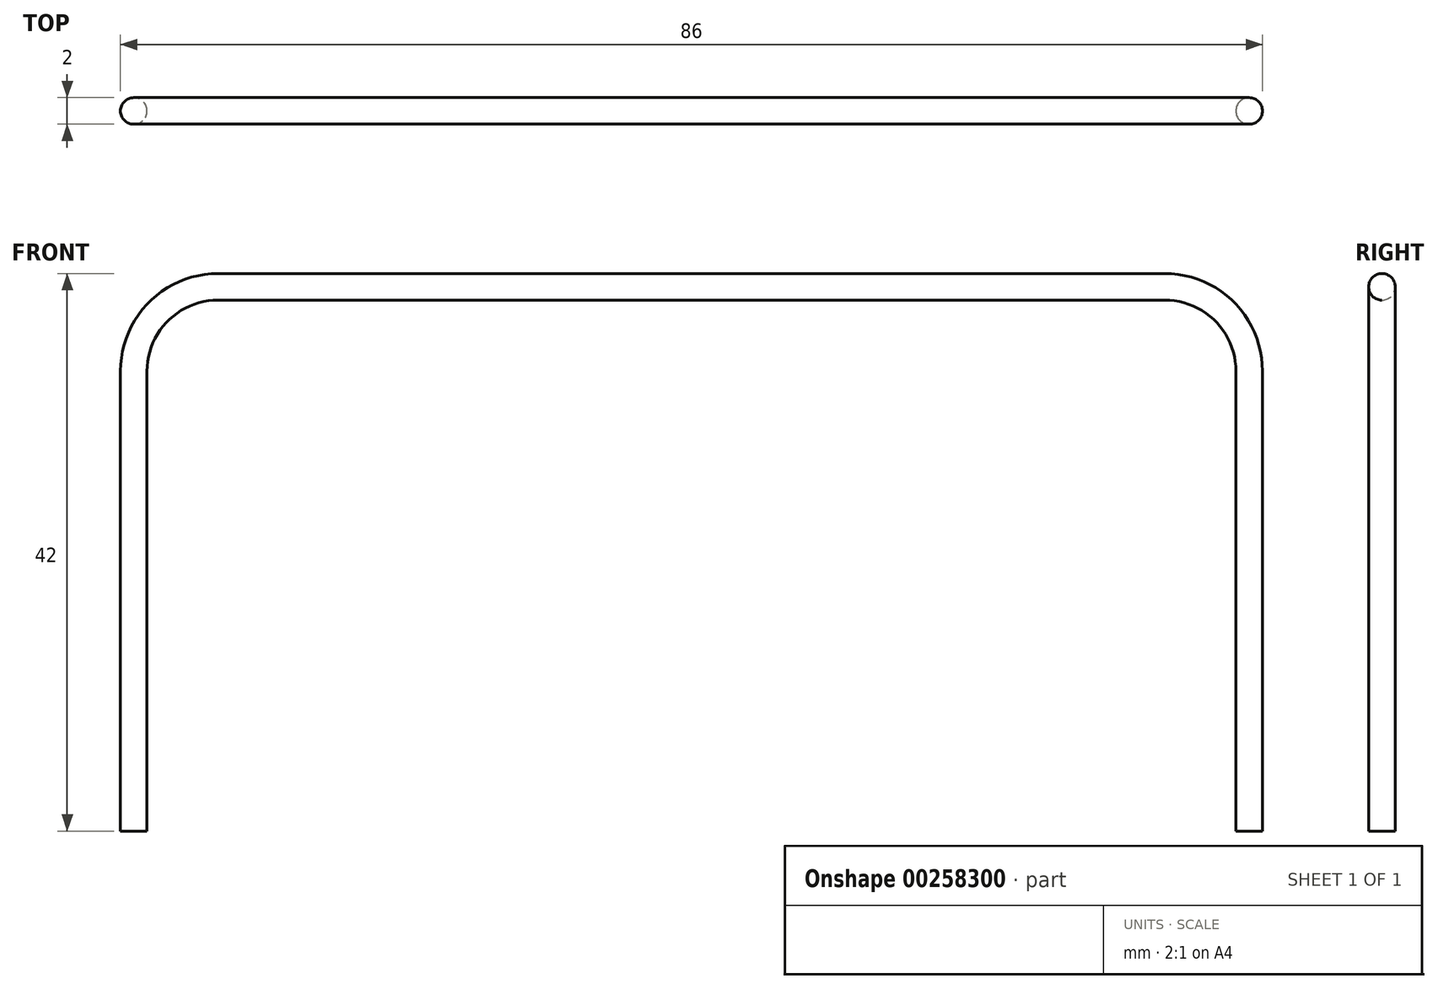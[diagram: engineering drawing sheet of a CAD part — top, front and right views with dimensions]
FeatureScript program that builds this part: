
annotation { "Feature Type Name" : "Feature", "Feature Type Description" : "" }
export const myFeature = defineFeature(function(context is Context, id is Id, definition is map)
    precondition{}
    {
        {
            var Q0;
            Q0=qCreatedBy(makeId("Front.planeOp"),FACE);
            var sketch = newSketch(context, id + "F0", { "sketchPlane" : qUnion([Q0])});
            skLineSegment(sketch, "E0", {"start": v(-42, 0) * mm, "end": v(-42, 34.65) * mm});
            skLineSegment(sketch, "E1", {"start": v(-35.65, 41) * mm, "end": v(0, 41) * mm});
            skPoint(sketch, "E2.visualSharp", {"position": v(-42, 41) * mm});
            skArc(sketch, "E2.filletArc", {"start": v(-35.65, 41) * mm, "mid": v(-40.14, 39.14) * mm, "end": v(-42, 34.65) * mm});
            skLineSegment(sketch, "E3.MirrorCS", {"start": v(35.65, 41) * mm, "end": v(0, 41) * mm});
            skArc(sketch, "E4.MirrorCS", {"start": v(35.65, 41) * mm, "mid": v(40.14, 39.14) * mm, "end": v(42, 34.65) * mm});
            skLineSegment(sketch, "E5.MirrorCS", {"start": v(42, 0) * mm, "end": v(42, 34.65) * mm});
            skSolve(sketch);
        }
        {
            var Q0;
            Q0=qCreatedBy(makeId("Top.planeOp"),FACE);
            var sketch = newSketch(context, id + "F1", { "sketchPlane" : qUnion([Q0])});
            skCircle(sketch, "E6", {"center": v(-42, 0) * mm, "radius": 1 * mm});
            skSolve(sketch);
        }
        {
            var Q0;
            Q0=makeQuery(id+"F1.imprint","IMPRINT",FACE,{"disambiguationData":[TD([[makeQuery(id+"F1.imprint","IMPRINT",EDGE,{"derivedFrom":sQuery(id+"F1.wireOp",EDGE,"E6")}),1.0]])]});
            var Q1;
            Q1=sQuery(id+"F0.wireOp",EDGE,"E0");
            var Q2;
            Q2=sQuery(id+"F0.wireOp",EDGE,"E2.filletArc");
            var Q3;
            Q3=sQuery(id+"F0.wireOp",EDGE,"E1");
            var Q4;
            Q4=sQuery(id+"F0.wireOp",EDGE,"E3.MirrorCS");
            var Q5;
            Q5=sQuery(id+"F0.wireOp",EDGE,"E4.MirrorCS");
            var Q6;
            Q6=sQuery(id+"F0.wireOp",EDGE,"E5.MirrorCS");
            sweep(context, id + "F2", {"profiles" : qUnion([Q0]), "path" : qUnion([Q1, Q2, Q3, Q4, Q5, Q6])});
        }
    });
